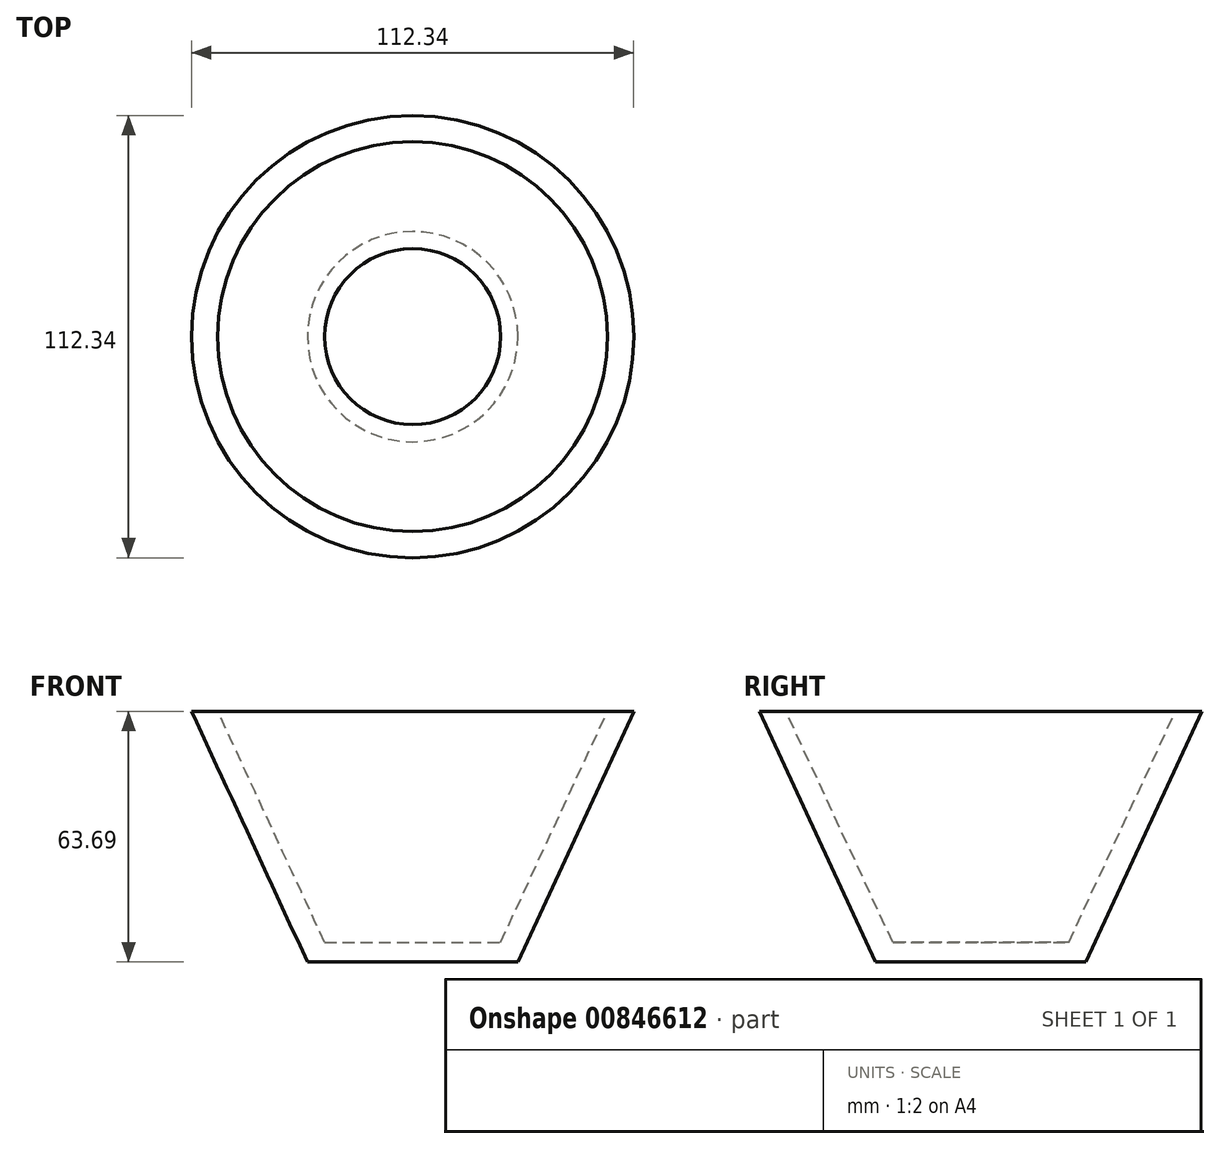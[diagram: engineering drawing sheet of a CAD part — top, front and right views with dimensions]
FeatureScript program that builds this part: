
annotation { "Feature Type Name" : "Feature", "Feature Type Description" : "" }
export const myFeature = defineFeature(function(context is Context, id is Id, definition is map)
    precondition{}
    {
        {
            var Q0;
            Q0=qCreatedBy(makeId("Front.planeOp"),FACE);
            var sketch = newSketch(context, id + "F0", { "sketchPlane" : qUnion([Q0])});
            skLineSegment(sketch, "E0", {"start": v(56.17, 28.43) * mm, "end": v(26.72, -35.26) * mm});
            skLineSegment(sketch, "E1", {"start": v(26.72, -35.26) * mm, "end": v(0, -35.26) * mm});
            skLineSegment(sketch, "E2", {"start": v(56.17, 28.43) * mm, "end": v(49.5, 28.43) * mm});
            skLineSegment(sketch, "E3", {"start": v(49.5, 28.43) * mm, "end": v(22.37, -30.26) * mm});
            skLineSegment(sketch, "E4", {"start": v(22.37, -30.26) * mm, "end": v(0, -30.26) * mm});
            skLineSegment(sketch, "E5", {"start": v(0, -35.26) * mm, "end": v(0, 30.65) * mm});
            skLineSegment(sketch, "E6", {"start": v(0, -30.26) * mm, "end": v(0, -35.26) * mm});
            skSolve(sketch);
        }
        {
            var Q0;
            Q0 = qSketchRegion(id + "F0", true);
            var Q1;
            Q1=sQuery(id+"F0.wireOp",EDGE,"E5");
            revolve(context, id + "F1", {"surfaceOperationType" : NewSurfaceOperationType.NEW, "entities" : qUnion([Q0]), "axis" : qUnion([Q1]), "revolveType" : RevolveType.FULL});
        }
    });
